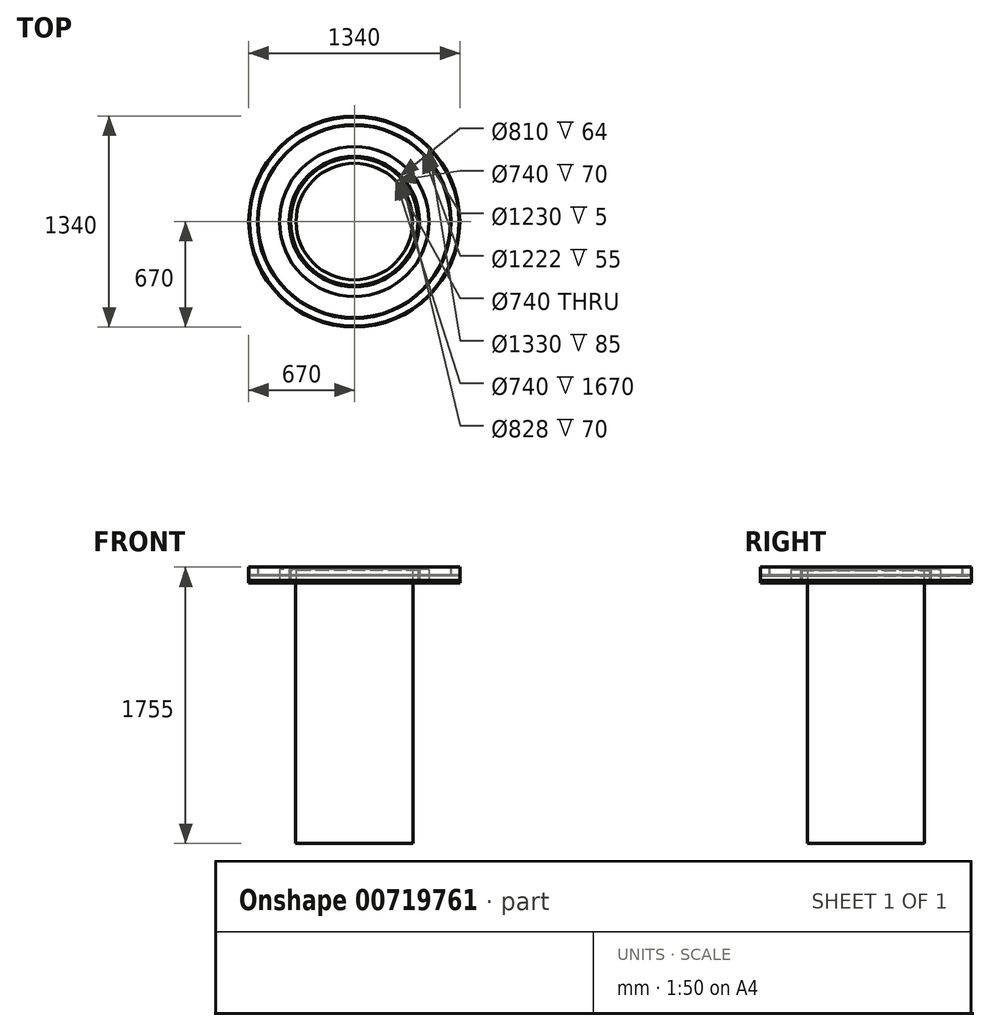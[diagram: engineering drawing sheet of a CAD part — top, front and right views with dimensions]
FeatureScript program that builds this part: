
annotation { "Feature Type Name" : "Feature", "Feature Type Description" : "" }
export const myFeature = defineFeature(function(context is Context, id is Id, definition is map)
    precondition{}
    {
        {
            var Q0;
            Q0=qCreatedBy(makeId("Top.planeOp"),FACE);
            var sketch = newSketch(context, id + "F0", { "sketchPlane" : qUnion([Q0])});
            skCircle(sketch, "E0", {"center": v(0, 0) * mm, "radius": 665 * mm});
            skCircle(sketch, "E1", {"center": v(0, 0) * mm, "radius": 370 * mm});
            skCircle(sketch, "E2", {"center": v(0, 0) * mm, "radius": 372.5 * mm});
            skSolve(sketch);
        }
        {
            var Q0;
            Q0=makeQuery(id+"F0.imprint","IMPRINT",FACE,{"disambiguationData":[TD([[makeQuery(id+"F0.imprint","IMPRINT",EDGE,{"derivedFrom":sQuery(id+"F0.wireOp",EDGE,"E0")}),1.0]])]});
            var sketch = newSketch(context, id + "F1", { "sketchPlane" : qUnion([Q0])});
            skCircle(sketch, "E3", {"center": v(0, 0) * mm, "radius": 370 * mm});
            skCircle(sketch, "E4", {"center": v(0, 0) * mm, "radius": 405 * mm});
            skSolve(sketch);
        }
        {
            var Q0;
            Q0 = qSketchRegion(id + "F1", true);
            extrude(context, id + "F2", {"entities" : qUnion([Q0]), "depth" : 70 * mm, "offsetDistance" : 25 * mm});
        }
        {
            var Q0;
            Q0=makeQuery(id+"F0.imprint","IMPRINT",FACE,{"disambiguationData":[TD([[makeQuery(id+"F0.imprint","IMPRINT",EDGE,{"derivedFrom":sQuery(id+"F0.wireOp",EDGE,"E2")}),1.0]])]});
            var sketch = newSketch(context, id + "F3", { "sketchPlane" : qUnion([Q0])});
            skCircle(sketch, "E5", {"center": v(0, 0) * mm, "radius": 414 * mm});
            skCircle(sketch, "E6", {"center": v(0, 0) * mm, "radius": 405 * mm});
            skSolve(sketch);
        }
        {
            var Q0;
            Q0 = qSketchRegion(id + "F3", true);
            extrude(context, id + "F4", {"entities" : qUnion([Q0]), "depth" : ((85 - 6) - (15)) * mm, "offsetDistance" : 25 * mm});
        }
        {
            var Q0;
            Q0=makeQuery(id+"F0.imprint","IMPRINT",FACE,{"disambiguationData":[TD([[makeQuery(id+"F0.imprint","IMPRINT",EDGE,{"derivedFrom":sQuery(id+"F0.wireOp",EDGE,"E1")}),1.0]])]});
            var sketch = newSketch(context, id + "F5", { "sketchPlane" : qUnion([Q0])});
            skCircle(sketch, "E7", {"center": v(0, 0) * mm, "radius": 475 * mm});
            skCircle(sketch, "E8", {"center": v(0, 0) * mm, "radius": 414 * mm});
            skSolve(sketch);
        }
        {
            var Q0;
            Q0 = qSketchRegion(id + "F5", true);
            extrude(context, id + "F6", {"entities" : qUnion([Q0]), "depth" : 70 * mm, "offsetDistance" : 25 * mm});
        }
        {
            var Q0;
            Q0=makeQuery(id+"F0.imprint","IMPRINT",FACE,{"disambiguationData":[TD([[makeQuery(id+"F0.imprint","IMPRINT",EDGE,{"derivedFrom":sQuery(id+"F0.wireOp",EDGE,"E1")}),1.0]])]});
            var sketch = newSketch(context, id + "F7", { "sketchPlane" : qUnion([Q0])});
            skCircle(sketch, "E9", {"center": v(0, 0) * mm, "radius": 670 * mm});
            skCircle(sketch, "E10", {"center": v(0, 0) * mm, "radius": 665 * mm});
            skSolve(sketch);
        }
        {
            var Q0;
            Q0=makeQuery(id+"F7.imprint","IMPRINT",FACE,{"disambiguationData":[TD([[makeQuery(id+"F7.imprint","IMPRINT",EDGE,{"derivedFrom":sQuery(id+"F7.wireOp",EDGE,"E9")}),1.0]])]});
            extrude(context, id + "F8", {"entities" : qUnion([Q0]), "depth" : (100 - 15) * mm, "offsetDistance" : 25 * mm});
        }
        {
            var Q0;
            Q0=makeQuery(id+"F0.imprint","IMPRINT",FACE,{"disambiguationData":[TD([[makeQuery(id+"F0.imprint","IMPRINT",EDGE,{"derivedFrom":sQuery(id+"F0.wireOp",EDGE,"E0")}),1.0]])]});
            cPlane(context, id + "F9", {"entities" : qUnion([Q0]), "cplaneType" : CPlaneType.OFFSET, "offset" : 30 * mm, "width" : 150 * mm, "height" : 150 * mm});
        }
        {
            var Q0;
            Q0=qCreatedBy(id+"F9.planeOp",FACE);
            var sketch = newSketch(context, id + "F10", { "sketchPlane" : qUnion([Q0])});
            skCircle(sketch, "E11", {"center": v(0, 0) * mm, "radius": 615 * mm});
            skCircle(sketch, "E12", {"center": v(0, 0) * mm, "radius": 611 * mm});
            skSolve(sketch);
        }
        {
            var Q0;
            Q0=makeQuery(id+"F10.imprint","IMPRINT",FACE,{"disambiguationData":[TD([[makeQuery(id+"F10.imprint","IMPRINT",EDGE,{"derivedFrom":sQuery(id+"F10.wireOp",EDGE,"E11")}),1.0]])]});
            extrude(context, id + "F11", {"entities" : qUnion([Q0]), "depth" : 55 * mm, "offsetDistance" : 25 * mm});
        }
        {
            var Q0;
            Q0=qCreatedBy(id+"F9.planeOp",FACE);
            var sketch = newSketch(context, id + "F12", { "sketchPlane" : qUnion([Q0])});
            skCircle(sketch, "E13", {"center": v(0, 0) * mm, "radius": 615 * mm});
            skCircle(sketch, "E14", {"center": v(0, 0) * mm, "radius": 665 * mm});
            skSolve(sketch);
        }
        {
            var Q0;
            Q0 = qSketchRegion(id + "F12", true);
            extrude(context, id + "F13", {"entities" : qUnion([Q0]), "depth" : 5 * mm, "offsetDistance" : 25 * mm});
        }
        {
            var Q0;
            Q0=makeQuery(id+"F0.imprint","IMPRINT",FACE,{"disambiguationData":[TD([[makeQuery(id+"F0.imprint","IMPRINT",EDGE,{"derivedFrom":sQuery(id+"F0.wireOp",EDGE,"E1")}),-1.0]])]});
            extrude(context, id + "F14", {"entities" : qUnion([Q0]), "oppositeDirection" : true, "depth" : (15 + 1655) * mm, "offsetDistance" : 25 * mm});
        }
        {
            var Q0;
            Q0=qCreatedBy(makeId("Top.planeOp"),FACE);
            cPlane(context, id + "F15", {"entities" : qUnion([Q0]), "cplaneType" : CPlaneType.OFFSET, "offset" : 15 * mm, "oppositeDirection" : true, "width" : 150 * mm, "height" : 150 * mm});
        }
        {
            var Q0;
            Q0=qCreatedBy(id+"F15.planeOp",FACE);
            var sketch = newSketch(context, id + "F16", { "sketchPlane" : qUnion([Q0])});
            skCircle(sketch, "E15", {"center": v(0, 0) * mm, "radius": 370 * mm});
            skCircle(sketch, "E16", {"center": v(0, 0) * mm, "radius": 670 * mm});
            skSolve(sketch);
        }
        {
            var Q0;
            Q0=makeQuery(id+"F16.imprint","IMPRINT",FACE,{"disambiguationData":[TD([[makeQuery(id+"F16.imprint","IMPRINT",EDGE,{"derivedFrom":sQuery(id+"F16.wireOp",EDGE,"E15")}),-1.0]])]});
            extrude(context, id + "F17", {"entities" : qUnion([Q0]), "depth" : 15 * mm, "offsetDistance" : 25 * mm});
        }
    });
